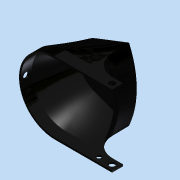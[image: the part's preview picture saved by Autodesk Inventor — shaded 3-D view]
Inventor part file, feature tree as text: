
AUTODESK INVENTOR PART (.ipt)
format: ipt  version: 2015 (Build 190159000, 159)  size: 539,136 bytes
history: native  units: in
note: dims shown in document units (in); Inventor stores cm internally (conversion verified against a paired STEP export)
features: sketch x11, extrude x8, other x4, plane x3, mirror x2, projected_geometry x2, loft x1, sweep x1
ambient origin geometry x8: Origin, YZ Plane, XZ Plane, XY Plane, X Axis, Y Axis, Z Axis, Center Point
bodies: Solid1 (feature_tree)
feature tree (32):
  other  "MotorMount.ipt"
  sketch  "Sketch2"  dims[d0=0.3937in d1=1.3189in]
  sketch  "Sketch3"  dims[d2=1.5748in d3=0.0625in]
  plane  "Work Plane1"
  loft  "Loft1"
  extrude  "Extrusion1"  Depth=0.0625in
  extrude  "Extrusion2"  TaperAngle=0.0deg  [1 undecoded]
  sketch  "Sketch6"  dims[d10=0.0in d11=0.0625in]
  extrude  "Extrusion3"  Depth=0.0625in
  plane  "Work Plane2"
  extrude  "Extrusion4"  Depth=0.0625in
  sketch  "Sketch8"  dims[d14=0.0625in d15=0.0in]
  extrude  "Extrusion5"  TaperAngle=0.0deg  [1 undecoded]
  extrude  "Extrusion6"  TaperAngle=0.0deg  [1 undecoded]
  plane  "Work Plane3"
  mirror  "Mirror1"
  extrude  "Extrusion7"  TaperAngle=0.0deg  [1 undecoded]
  mirror  "Mirror2"
  sketch  "Sketch10"  dims[d18=0.1339in d19=0.1339in]
  sweep  "Sweep2"
  extrude  "Extrusion8"  Depth=0.1339in
  other  "TaggingFeature1"
  sketch  "Sketch4"  dims[d4=0.0625in d5=0.0in d6=90.0deg]
  sketch  "Sketch5"  dims[d7=0.0in d8=90.0deg d9=0.0625in]
  sketch  "Sketch7"  dims[d12=0.0625in d13=0.0in]
  sketch  "Sketch9"  dims[d16=0.0625in d17=0.0in]
  projected_geometry  "Projected Loop1"
  projected_geometry  "Projected Loop2"
  sketch  "Sketch11"  dims[d20=0.1339in d21=0.1339in d22=0.1969in d23=0.1969in d24=0.1969in d25=0.1969in d26=0.1412in d27=0.0in d28=0.0625in d29=0.0in d31=0.75in d32=0.0625in d33=0.0in d34=0.96in d35=0.96in d36=0.0625in d39=0.0in d40=0.0in d41=0.5in d42=0.0in d44=0.205in d45=0.205in d46=0.1575in]
  sketch  "3D Sketch2"
  other  "Solid2::MotorMount.ipt"
  other  "Srf1"
note: 4 required parameter values undecoded (feature->parameter linkage not recoverable at this tier; creation-order binding heuristic only, values carry confidence <= 0.55)
